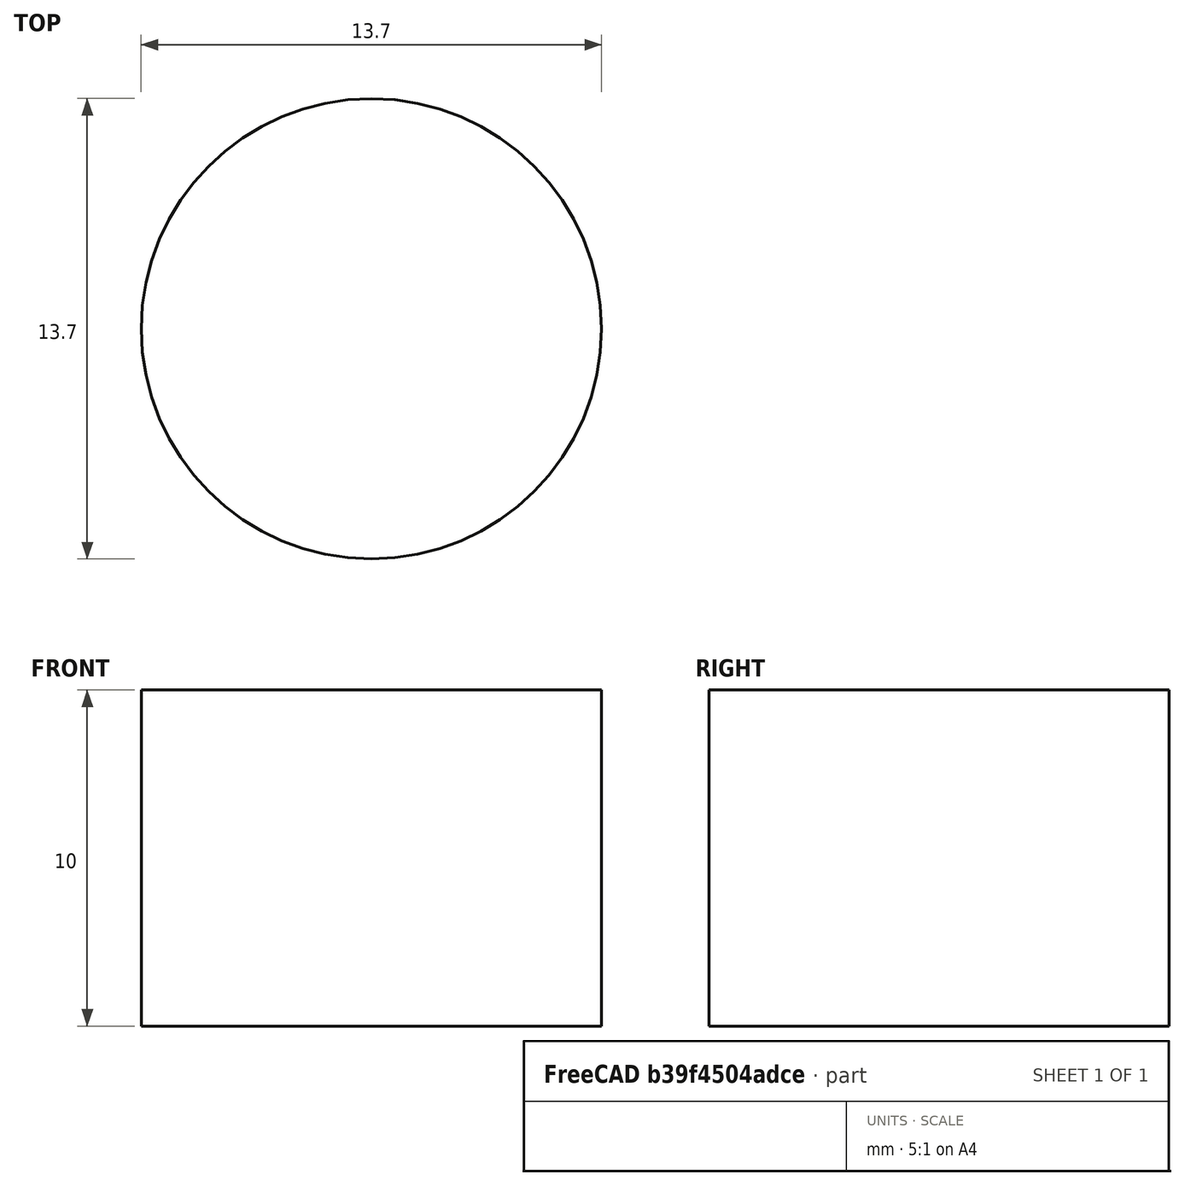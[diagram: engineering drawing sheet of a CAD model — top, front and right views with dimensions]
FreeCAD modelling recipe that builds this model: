
FCSTD DOCUMENT  (FreeCAD 0.18R4 (GitTag))
Label: asdf
License: All rights reserved
LicenseURL: http://en.wikipedia.org/wiki/All_rights_reserved
objects: Sketcher::SketchObject×5, PartDesign::Pad×1, PartDesign::Plane×1, PartDesign::Body×1, App::MeasureDistance×1
note: 9 computed .brp shape members not serialized (recipe doc carries the construction recipe); baked Part::Feature solids carry a one-line shape summary decoded from their .brp

FEATURE [Sketcher::SketchObject] Sketch
  MapMode = 5
  Support = -> [XY_Plane]
  sketch-geometry (1):
    g0: Circle CenterX=-2.93782 CenterY=2.10874 CenterZ=0 NormalX=0 NormalY=0 NormalZ=1 AngleXU=0 Radius=6.84719
FEATURE [PartDesign::Pad] Pad
  Length = 10
  Length2 = 100
  Profile = -> Sketch
  Type = 0
FEATURE [PartDesign::Plane] DatumPlane
  Length = 24
  MapMode = 2
  ResizeMode = 0
  Support = -> [Sketch]
  Width = 24
FEATURE [PartDesign::Body] Body
  Group = -> [Sketch,Pad,DatumPlane]
  Origin = -> Origin
  Tip = -> Pad
FEATURE [Sketcher::SketchObject] Sketch001
FEATURE [Sketcher::SketchObject] Sketch002
  MapMode = 5
  Placement = pos=(0,0,10) rot=(0,0,1;0rad)
  Support = -> [Pad]
  sketch-geometry (1):
    g0: Circle CenterX=-3.51718 CenterY=2.47513 CenterZ=0 NormalX=0 NormalY=0 NormalZ=1 AngleXU=0 Radius=1.52114
FEATURE [Sketcher::SketchObject] Sketch003
  Placement = pos=(0,0,0) rot=(-1,0,0;4.71239rad)
  sketch-geometry (10):
    g0: Circle CenterX=-2.66482 CenterY=17.8394 CenterZ=0 NormalX=0 NormalY=0 NormalZ=1 AngleXU=0 Radius=8.00352
    g1: LineSegment StartX=-7.49638 StartY=20.792 StartZ=0 EndX=-5.95296 EndY=22.2012 EndZ=0
    g2: LineSegment StartX=-5.95296 StartY=22.2012 StartZ=0 EndX=-3.47008 EndY=23.2749 EndZ=0
    g3: LineSegment StartX=-3.47008 StartY=23.2749 StartZ=0 EndX=-1.38983 EndY=23.1407 EndZ=0
    g4: LineSegment StartX=-1.38983 StartY=23.1407 StartZ=0 EndX=0.757533 EndY=22.2012 EndZ=0
    g5: LineSegment StartX=0.757533 StartY=22.2012 StartZ=0 EndX=1.89832 EndY=20.9933 EndZ=0
    g6: LineSegment StartX=1.89832 StartY=20.9933 StartZ=0 EndX=2.50226 EndY=19.9868 EndZ=0
    g7: LineSegment StartX=-7.42927 StartY=15.4907 StartZ=0 EndX=-4.94639 EndY=14.2828 EndZ=0
    g8: LineSegment StartX=0.086481 StartY=14.0815 StartZ=0 EndX=2.23384 EndY=15.4907 EndZ=0
    g9: LineSegment StartX=-6.22138 StartY=16.6986 StartZ=0 EndX=-4.67797 EndY=16.6315 EndZ=0
  constraints (5):
    c: Coincident(g1,g2)
    c: Coincident(g2,g3)
    c: Coincident(g3,g4)
    c: Coincident(g4,g5)
    c: Coincident(g5,g6)
FEATURE [Sketcher::SketchObject] Sketch004
  Placement = pos=(0,0,0) rot=(0.57735,0.57735,0.57735;2.0944rad)
  sketch-geometry (1):
    g0: LineSegment StartX=-8.38777 StartY=-0.219795 StartZ=0 EndX=-8.38777 EndY=5.90333 EndZ=0
FEATURE [App::MeasureDistance] Distance  label="Distance: 13.07 mm"
  Distance = 13.0666
  P1 = (-3.30574,-4.71852,9.191)
  P2 = (-2.37531,4.52245,0)
